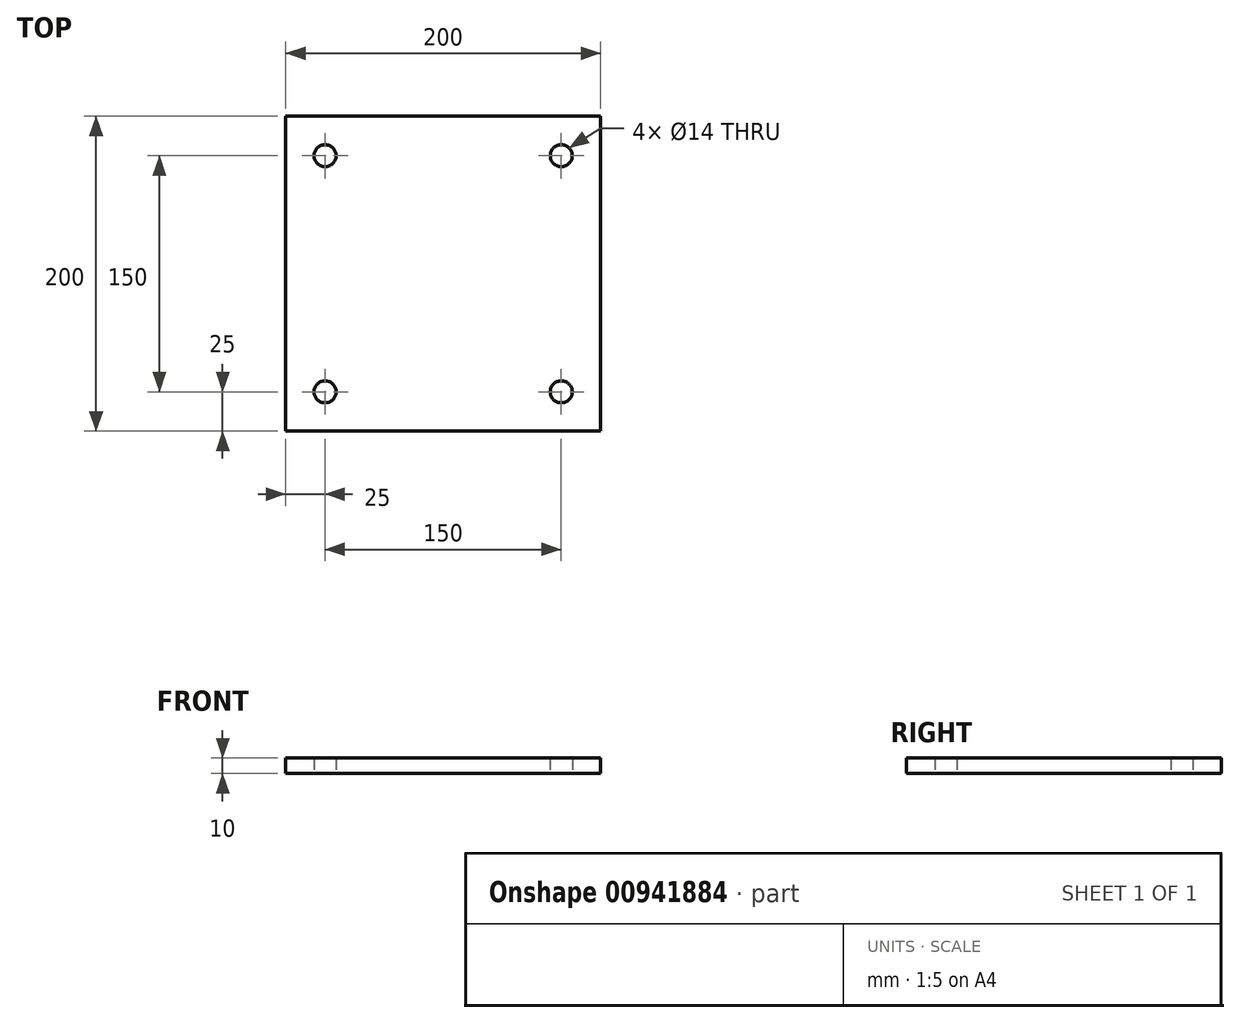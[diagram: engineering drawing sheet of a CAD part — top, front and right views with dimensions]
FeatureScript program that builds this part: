
annotation { "Feature Type Name" : "Feature", "Feature Type Description" : "" }
export const myFeature = defineFeature(function(context is Context, id is Id, definition is map)
    precondition{}
    {
        {
            var Q0;
            Q0=qCreatedBy(makeId("Top.planeOp"),FACE);
            var sketch = newSketch(context, id + "F0", { "sketchPlane" : qUnion([Q0])});
            skLineSegment(sketch, "E0.bottom", {"start": v(100, 100) * mm, "end": v(-100, 100) * mm});
            skLineSegment(sketch, "E0.top", {"start": v(100, -100) * mm, "end": v(-100, -100) * mm});
            skLineSegment(sketch, "E0.left", {"start": v(100, 100) * mm, "end": v(100, -100) * mm});
            skLineSegment(sketch, "E0.right", {"start": v(-100, 100) * mm, "end": v(-100, -100) * mm});
            skPoint(sketch, "E0.middle", {"position": v(0, 0) * mm});
            skCircle(sketch, "E1", {"center": v(-75, 75) * mm, "radius": 7 * mm});
            skCircle(sketch, "E2", {"center": v(75, 75) * mm, "radius": 7 * mm});
            skCircle(sketch, "E3", {"center": v(-75, -75) * mm, "radius": 7 * mm});
            skCircle(sketch, "E4", {"center": v(75, -75) * mm, "radius": 7 * mm});
            skSolve(sketch);
        }
        {
            var Q0;
            Q0=makeQuery(id+"F0.imprint","IMPRINT",FACE,{"disambiguationData":[TD([[makeQuery(id+"F0.imprint","IMPRINT",EDGE,{"derivedFrom":sQuery(id+"F0.wireOp",EDGE,"E0.bottom")}),1.0]])]});
            extrude(context, id + "F1", {"entities" : qUnion([Q0]), "depth" : 10 * mm, "offsetDistance" : 25 * mm});
        }
    });
